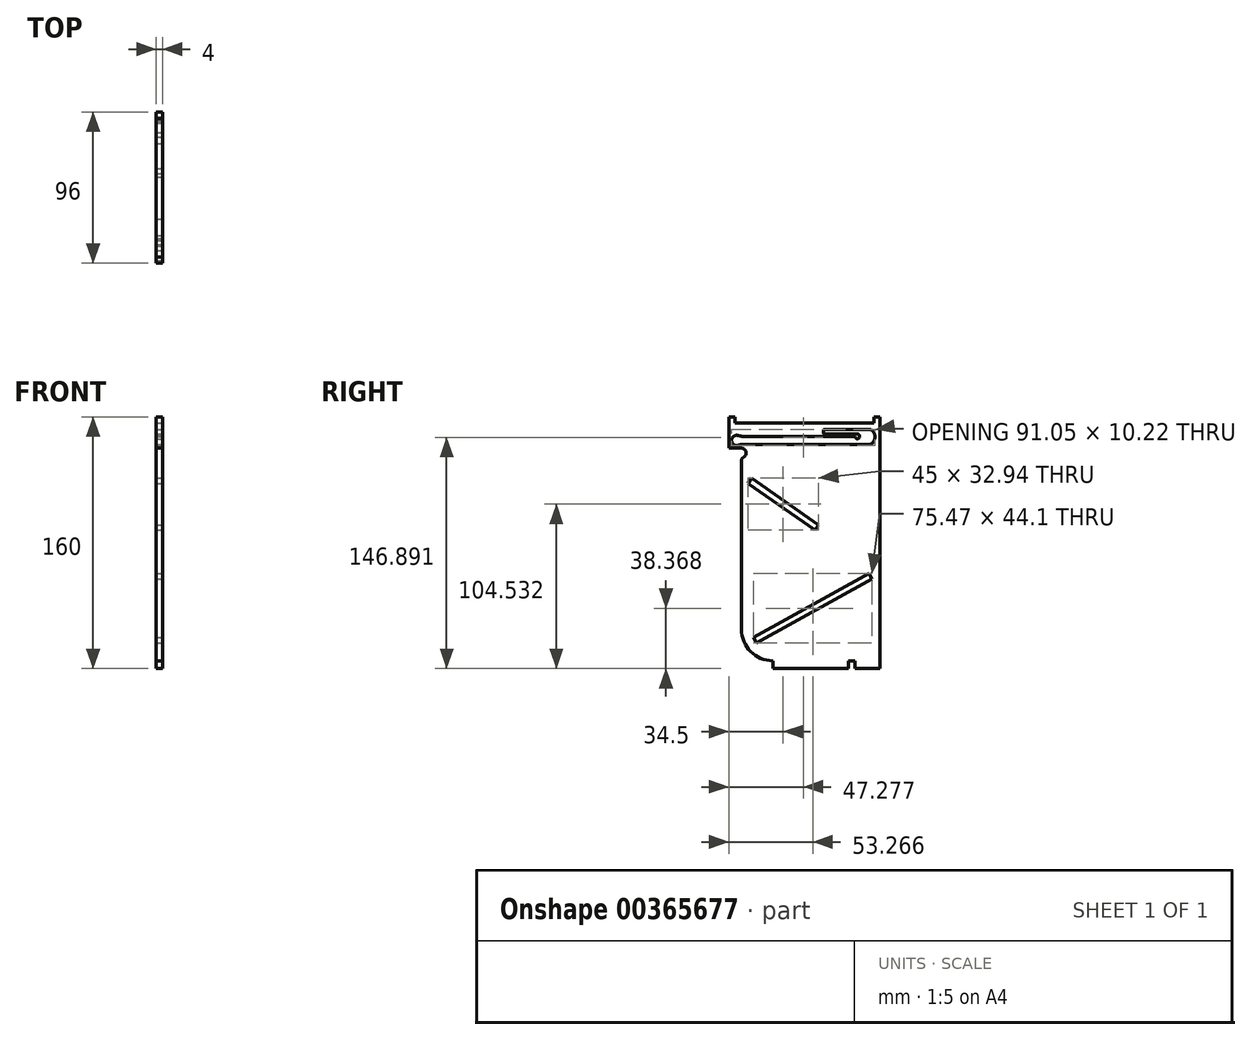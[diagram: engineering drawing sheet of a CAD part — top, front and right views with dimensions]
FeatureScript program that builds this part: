
annotation { "Feature Type Name" : "Feature", "Feature Type Description" : "" }
export const myFeature = defineFeature(function(context is Context, id is Id, definition is map)
    precondition{}
    {
        {
            var Q0;
            Q0=qCreatedBy(makeId("Right.planeOp"),FACE);
            var sketch = newSketch(context, id + "F0", { "sketchPlane" : qUnion([Q0])});
            skLineSegment(sketch, "E0.bottom", {"start": v(0, 0) * mm, "end": v(96, 0) * mm});
            skLineSegment(sketch, "E0.top", {"start": v(0, 160) * mm, "end": v(96, 160) * mm});
            skLineSegment(sketch, "E0.left", {"start": v(0, 0) * mm, "end": v(0, 160) * mm});
            skLineSegment(sketch, "E0.right", {"start": v(96, 0) * mm, "end": v(96, 160) * mm});
            skPoint(sketch, "E1.visualSharp", {"position": v(0, 0) * mm});
            skSolve(sketch);
        }
        {
            var Q0;
            Q0 = qSketchRegion(id + "F0", true);
            extrude(context, id + "F1", {"entities" : qUnion([Q0]), "depth" : 4 * mm});
        }
        {
            var Q0;
            Q0=makeQuery(id+"F1.opExtrude","CAP_FACE",FACE,{"disambiguationData":[OSD([sQuery(id+"F0.wireOp",EDGE,"E0.bottom"),sQuery(id+"F0.wireOp",EDGE,"E0.top"),sQuery(id+"F0.wireOp",EDGE,"E0.left"),sQuery(id+"F0.wireOp",EDGE,"E0.right")])],"isStart":false});
            var sketch = newSketch(context, id + "F2", { "sketchPlane" : qUnion([Q0])});
            skLineSegment(sketch, "E2.bottom", {"start": v(80, 0) * mm, "end": v(76, 0) * mm});
            skLineSegment(sketch, "E2.left", {"start": v(80, 0) * mm, "end": v(80, 5) * mm});
            skLineSegment(sketch, "E2.right", {"start": v(76, 0) * mm, "end": v(76, 5) * mm});
            skLineSegment(sketch, "E3", {"start": v(76, 5) * mm, "end": v(80, 5) * mm});
            skLineSegment(sketch, "E4.bottom", {"start": v(92, 160) * mm, "end": v(4, 160) * mm});
            skLineSegment(sketch, "E4.top", {"start": v(92, 156) * mm, "end": v(4, 156) * mm});
            skLineSegment(sketch, "E4.left", {"start": v(92, 160) * mm, "end": v(92, 156) * mm});
            skLineSegment(sketch, "E4.right", {"start": v(4, 160) * mm, "end": v(4, 156) * mm});
            skSolve(sketch);
        }
        {
            var Q0;
            Q0 = qSketchRegion(id + "F2", true);
            extrude(context, id + "F3", {"entities" : qUnion([Q0]), "operationType" : NewBodyOperationType.REMOVE, "endBound" : BoundingType.UP_TO_NEXT, "oppositeDirection" : true, "depth" : 25 * mm});
        }
        {
            var Q0;
            Q0=makeQuery(id+"F1.opExtrude","CAP_FACE",FACE,{"disambiguationData":[OSD([sQuery(id+"F0.wireOp",EDGE,"E0.bottom"),sQuery(id+"F0.wireOp",EDGE,"E0.top"),sQuery(id+"F0.wireOp",EDGE,"E0.left"),sQuery(id+"F0.wireOp",EDGE,"E0.right")])],"isStart":false});
            var sketch = newSketch(context, id + "F4", { "sketchPlane" : qUnion([Q0])});
            skPoint(sketch, "E5.endSnap0", {"position": v(88, 0) * mm});
            skLineSegment(sketch, "E6", {"start": v(57, 91.35) * mm, "end": v(14.28, 121) * mm});
            skLineSegment(sketch, "E7", {"start": v(14.28, 121) * mm, "end": v(12, 117.71) * mm});
            skLineSegment(sketch, "E8", {"start": v(12, 117.71) * mm, "end": v(54.72, 88.06) * mm});
            skLineSegment(sketch, "E9", {"start": v(54.72, 88.06) * mm, "end": v(57, 91.35) * mm});
            skLineSegment(sketch, "E10", {"start": v(15.53, 19.82) * mm, "end": v(89.07, 60.42) * mm});
            skLineSegment(sketch, "E11", {"start": v(89.07, 60.42) * mm, "end": v(91, 56.92) * mm});
            skLineSegment(sketch, "E12", {"start": v(91, 56.92) * mm, "end": v(17.47, 16.32) * mm});
            skLineSegment(sketch, "E13", {"start": v(17.47, 16.32) * mm, "end": v(15.53, 19.82) * mm});
            skLineSegment(sketch, "E14", {"start": v(19.03, 21.75) * mm, "end": v(20.97, 18.25) * mm, "construction": true});
            skPoint(sketch, "E15", {"position": v(20, 20) * mm});
            skSolve(sketch);
        }
        {
            var Q0;
            Q0 = qSketchRegion(id + "F4", true);
            extrude(context, id + "F5", {"entities" : qUnion([Q0]), "operationType" : NewBodyOperationType.REMOVE, "endBound" : BoundingType.UP_TO_NEXT, "oppositeDirection" : true, "depth" : 25 * mm});
        }
        {
            var Q0;
            Q0=makeQuery(id+"F1.opExtrude","CAP_FACE",FACE,{"disambiguationData":[OSD([sQuery(id+"F0.wireOp",EDGE,"E0.bottom"),sQuery(id+"F0.wireOp",EDGE,"E0.top"),sQuery(id+"F0.wireOp",EDGE,"E0.left"),sQuery(id+"F0.wireOp",EDGE,"E0.right")])],"isStart":false});
            var sketch = newSketch(context, id + "F6", { "sketchPlane" : qUnion([Q0])});
            skLineSegment(sketch, "E16", {"start": v(0, 0) * mm, "end": v(0, 140) * mm});
            skLineSegment(sketch, "E17", {"start": v(0, 140) * mm, "end": v(8, 140) * mm});
            skLineSegment(sketch, "E18", {"start": v(8, 140) * mm, "end": v(8, 25) * mm});
            skArc(sketch, "E19", {"start": v(8, 25) * mm, "mid": v(13.86, 10.86) * mm, "end": v(28, 5) * mm});
            skLineSegment(sketch, "E20", {"start": v(0, 0) * mm, "end": v(28, 0) * mm});
            skLineSegment(sketch, "E21", {"start": v(28, 5) * mm, "end": v(28, 0) * mm});
            skSolve(sketch);
        }
        {
            var Q0;
            Q0 = qSketchRegion(id + "F6", true);
            var Q1;
            {var subQ1=sQuery(id+"F6.wireOp",EDGE,"E16");Q1=makeQuery(id+"F6.imprint","IMPRINT",FACE,{"disambiguationData":[TD([[makeQuery(id+"F6.imprint","IMPRINT",EDGE,{"derivedFrom":subQ1}),-1.0]])]});}
            extrude(context, id + "F7", {"entities" : qUnion([Q0, Q1]), "operationType" : NewBodyOperationType.REMOVE, "endBound" : BoundingType.UP_TO_NEXT, "oppositeDirection" : true, "depth" : 25 * mm});
        }
        {
            var Q0;
            Q0=makeQuery(id+"F1.opExtrude","CAP_FACE",FACE,{"disambiguationData":[OSD([sQuery(id+"F0.wireOp",EDGE,"E0.bottom"),sQuery(id+"F0.wireOp",EDGE,"E0.top"),sQuery(id+"F0.wireOp",EDGE,"E0.left"),sQuery(id+"F0.wireOp",EDGE,"E0.right")])],"isStart":false});
            var sketch = newSketch(context, id + "F8", { "sketchPlane" : qUnion([Q0])});
            skLineSegment(sketch, "E22", {"start": v(9.4, 142.5) * mm, "end": v(90.08, 142.5) * mm});
            skLineSegment(sketch, "E23", {"start": v(90.08, 142.5) * mm, "end": v(90.08, 147.5) * mm, "construction": true});
            skLineSegment(sketch, "E24", {"start": v(90.08, 147.5) * mm, "end": v(90.08, 152) * mm, "construction": true});
            skLineSegment(sketch, "E25", {"start": v(90.08, 152) * mm, "end": v(60.08, 152) * mm});
            skLineSegment(sketch, "E26", {"start": v(60.08, 152) * mm, "end": v(60.08, 150) * mm});
            skLineSegment(sketch, "E27", {"start": v(61.08, 149) * mm, "end": v(81.58, 149) * mm});
            skLineSegment(sketch, "E28", {"start": v(9.4, 147.5) * mm, "end": v(80.08, 147.5) * mm});
            skArc(sketch, "E29", {"start": v(80.08, 147.5) * mm, "mid": v(82.64, 146.44) * mm, "end": v(81.58, 149) * mm});
            skArc(sketch, "E30", {"start": v(90.08, 142.5) * mm, "mid": v(92.8, 147.25) * mm, "end": v(90.08, 152) * mm});
            skPoint(sketch, "E31.visualSharp", {"position": v(60.08, 149) * mm});
            skArc(sketch, "E31.filletArc", {"start": v(60.08, 150) * mm, "mid": v(60.37, 149.3) * mm, "end": v(61.08, 149) * mm});
            skArc(sketch, "E32", {"start": v(6.08, 148.07) * mm, "mid": v(1.75, 145) * mm, "end": v(6.08, 141.93) * mm});
            skPoint(sketch, "E33.visualSharp", {"position": v(7.08, 147.5) * mm});
            skArc(sketch, "E33.filletArc", {"start": v(6.08, 148.07) * mm, "mid": v(7.71, 147.64) * mm, "end": v(9.4, 147.5) * mm});
            skPoint(sketch, "E34.visualSharp", {"position": v(7.08, 142.5) * mm});
            skArc(sketch, "E34.filletArc", {"start": v(9.4, 142.5) * mm, "mid": v(7.71, 142.36) * mm, "end": v(6.08, 141.93) * mm});
            skSolve(sketch);
        }
        {
            var Q0;
            Q0 = qSketchRegion(id + "F8", true);
            extrude(context, id + "F9", {"entities" : qUnion([Q0]), "operationType" : NewBodyOperationType.REMOVE, "endBound" : BoundingType.THROUGH_ALL, "oppositeDirection" : true, "depth" : 25 * mm});
        }
        {
            var Q0;
            Q0=makeQuery(id+"F1.opExtrude","CAP_FACE",FACE,{"disambiguationData":[OSD([sQuery(id+"F0.wireOp",EDGE,"E0.bottom"),sQuery(id+"F0.wireOp",EDGE,"E0.top"),sQuery(id+"F0.wireOp",EDGE,"E0.left"),sQuery(id+"F0.wireOp",EDGE,"E0.right")])],"isStart":false});
            var sketch = newSketch(context, id + "F10", { "sketchPlane" : qUnion([Q0])});
            skArc(sketch, "E35", {"start": v(8, 140) * mm, "mid": v(10.91, 137.73) * mm, "end": v(9.41, 134.35) * mm});
            skArc(sketch, "E36", {"start": v(9.41, 134.35) * mm, "mid": v(8.38, 133.37) * mm, "end": v(8, 132) * mm});
            skLineSegment(sketch, "E37", {"start": v(8, 140) * mm, "end": v(8, 132) * mm});
            skSolve(sketch);
        }
        {
            var Q0;
            Q0 = qSketchRegion(id + "F10", true);
            extrude(context, id + "F11", {"entities" : qUnion([Q0]), "operationType" : NewBodyOperationType.REMOVE, "endBound" : BoundingType.UP_TO_NEXT, "oppositeDirection" : true, "depth" : 25 * mm});
        }
    });
